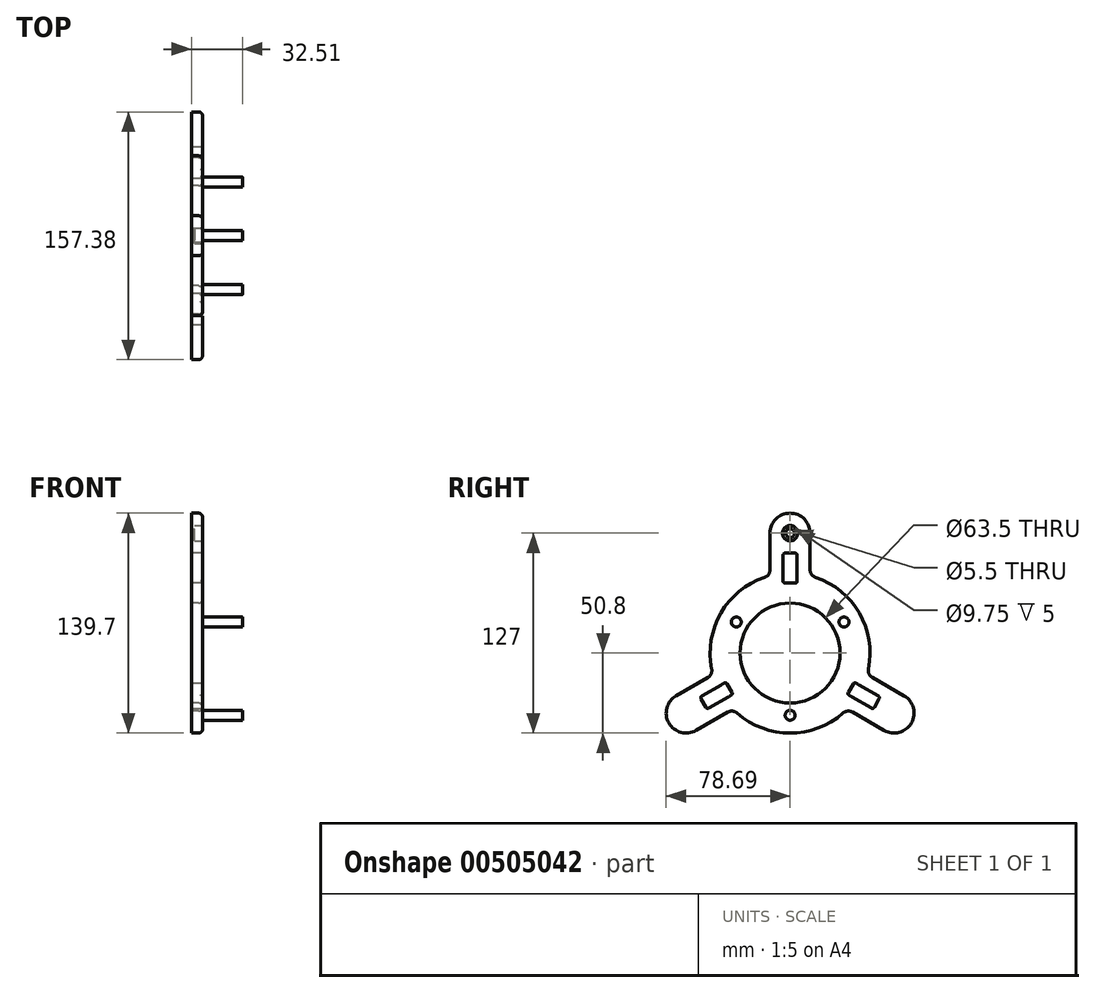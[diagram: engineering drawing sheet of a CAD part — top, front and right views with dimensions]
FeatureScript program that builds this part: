
annotation { "Feature Type Name" : "Feature", "Feature Type Description" : "" }
export const myFeature = defineFeature(function(context is Context, id is Id, definition is map)
    precondition{}
    {
        {
            var Q0;
            Q0=qCreatedBy(makeId("Right.planeOp"),FACE);
            var sketch = newSketch(context, id + "F0", { "sketchPlane" : qUnion([Q0])});
            skCircle(sketch, "E0", {"center": v(0, 0) * mm, "radius": 50.8 * mm});
            skCircle(sketch, "E1", {"center": v(0, 76.2) * mm, "radius": 12.7 * mm});
            skLineSegment(sketch, "E2", {"start": v(12.7, 76.2) * mm, "end": v(12.7, 49.19) * mm});
            skLineSegment(sketch, "E3", {"start": v(-12.7, 76.2) * mm, "end": v(-12.7, 49.19) * mm});
            skCircle(sketch, "E4", {"center": v(0, 0) * mm, "radius": 31.75 * mm});
            skLineSegment(sketch, "E5", {"start": v(0, 76.2) * mm, "end": v(0, 31.75) * mm});
            skLineSegment(sketch, "E6.bottom", {"start": v(4.45, 63.5) * mm, "end": v(-4.45, 63.5) * mm});
            skLineSegment(sketch, "E6.top", {"start": v(4.45, 44.45) * mm, "end": v(-4.45, 44.45) * mm});
            skLineSegment(sketch, "E6.left", {"start": v(4.45, 63.5) * mm, "end": v(4.45, 44.45) * mm});
            skLineSegment(sketch, "E6.right", {"start": v(-4.45, 63.5) * mm, "end": v(-4.45, 44.45) * mm});
            skPoint(sketch, "E6.middle", {"position": v(0, 53.98) * mm});
            skSolve(sketch);
        }
        {
            var Q0;
            {var subQ0=sQuery(id+"F0.wireOp",EDGE,"E0");var subQ1=makeQuery(id+"F0.imprint","INTERSECT",VERTEX,{"derivedFrom":[subQ0,sQuery(id+"F0.wireOp",EDGE,"E2")]});Q0=makeQuery(id+"F0.imprint","IMPRINT",FACE,{"disambiguationData":[TD([[makeQuery(id+"F0.imprint","IMPRINT",EDGE,{"disambiguationData":[TD([[subQ1,-1.0]])],"derivedFrom":subQ0}),1.0]])]});}
            var Q1;
            {var subQ0=sQuery(id+"F0.wireOp",EDGE,"E2");Q1=makeQuery(id+"F0.imprint","IMPRINT",FACE,{"disambiguationData":[TD([[makeQuery(id+"F0.imprint","IMPRINT",EDGE,{"derivedFrom":subQ0}),-1.0]])]});}
            var Q2;
            {var subQ0=sQuery(id+"F0.wireOp",EDGE,"E1");var subQ1=makeQuery(id+"F0.imprint","INTERSECT",VERTEX,{"derivedFrom":[subQ0,sQuery(id+"F0.wireOp",EDGE,"E2")]});Q2=makeQuery(id+"F0.imprint","IMPRINT",FACE,{"disambiguationData":[TD([[makeQuery(id+"F0.imprint","IMPRINT",EDGE,{"disambiguationData":[TD([[subQ1,-1.0]])],"derivedFrom":subQ0}),1.0]])]});}
            var Q3;
            {var subQ0=sQuery(id+"F0.wireOp",EDGE,"b7OHnpGz-8ywc-knMQ-bxzY-wuBPayrR5RMl");Q3=makeQuery(id+"F0.imprint","IMPRINT",FACE,{"disambiguationData":[TD([[makeQuery(id+"F0.imprint","IMPRINT",EDGE,{"derivedFrom":subQ0}),1.0]])]});}
            var Q4;
            {var subQ0=sQuery(id+"F0.wireOp",EDGE,"xrwcpAAF-OSON-ZUx1-X68L-PDSKPu6AwuQr");var subQ1=makeQuery(id+"F0.imprint","INTERSECT",VERTEX,{"derivedFrom":[subQ0,sQuery(id+"F0.wireOp",EDGE,"b7OHnpGz-8ywc-knMQ-bxzY-wuBPayrR5RMl")]});Q4=makeQuery(id+"F0.imprint","IMPRINT",FACE,{"disambiguationData":[TD([[makeQuery(id+"F0.imprint","IMPRINT",EDGE,{"disambiguationData":[TD([[subQ1,-1.0]])],"derivedFrom":subQ0}),1.0]])]});}
            var Q5;
            {var subQ0=sQuery(id+"F0.wireOp",EDGE,"RlsfpPi4-7fas-HaKM-YI3l-A7btP1uvOqbB");Q5=makeQuery(id+"F0.imprint","IMPRINT",FACE,{"disambiguationData":[TD([[makeQuery(id+"F0.imprint","IMPRINT",EDGE,{"derivedFrom":subQ0}),1.0]])]});}
            var Q6;
            {var subQ5=sQuery(id+"F0.wireOp",EDGE,"6OggtRER-jhK3-v4md-decp-ikiG6QNqgnZd");Q6=makeQuery(id+"F0.imprint","IMPRINT",FACE,{"disambiguationData":[TD([[makeQuery(id+"F0.imprint","IMPRINT",EDGE,{"derivedFrom":subQ5}),1.0]])]});}
            var Q7;
            {var subQ5=sQuery(id+"F0.wireOp",EDGE,"FEhqOE9T-DJEj-I29Y-v5rS-7Lfa6DwVfN2z.bottom");Q7=makeQuery(id+"F0.imprint","IMPRINT",FACE,{"disambiguationData":[TD([[makeQuery(id+"F0.imprint","IMPRINT",EDGE,{"derivedFrom":subQ5}),1.0]])]});}
            var Q8;
            {var subQ0=sQuery(id+"F0.wireOp",EDGE,"E3");Q8=makeQuery(id+"F0.imprint","IMPRINT",FACE,{"disambiguationData":[TD([[makeQuery(id+"F0.imprint","IMPRINT",EDGE,{"derivedFrom":subQ0}),1.0]])]});}
            extrude(context, id + "F1", {"entities" : qUnion([Q0, Q1, Q2, Q3, Q4, Q5, Q6, Q7, Q8]), "depth" : 7.11 * mm});
        }
        {
            var Q0;
            Q0=makeQuery(id+"F1.opExtrude","CAP_FACE",FACE,{"disambiguationData":[OSD([sQuery(id+"F0.wireOp",EDGE,"E0"),sQuery(id+"F0.wireOp",EDGE,"E1"),sQuery(id+"F0.wireOp",EDGE,"E2"),sQuery(id+"F0.wireOp",EDGE,"E3")])],"isStart":false});
            var sketch = newSketch(context, id + "F2", { "sketchPlane" : qUnion([Q0])});
            skPoint(sketch, "E7", {"position": v(0, 76.2) * mm});
            skSolve(sketch);
        }
        {
            var Q0;
            Q0=sQuery(id+"F2.wireOp",VERTEX,"E7");
            var Q1;
            Q1=makeQuery(id+"F1.opExtrude","SWEPT_BODY",BODY,{"disambiguationData":[OSD([sQuery(id+"F0.wireOp",EDGE,"E0"),sQuery(id+"F0.wireOp",EDGE,"E1"),sQuery(id+"F0.wireOp",EDGE,"E2"),sQuery(id+"F0.wireOp",EDGE,"E3")])]});
            hole(context, id + "F3", {"style" : HoleStyle.C_BORE, "endStyle" : HoleEndStyle.THROUGH, "standardTappedOrClearance" : lookupTablePath({ "standard" : "ISO", "fit" : "Normal", "size" : "M5", "type" : "Clearance" }), "standardBlindInLast" : lookupTablePath({ "fit" : "Standard", "standard" : "ISO", "size" : "M5", "type" : "Clearance" }), "holeDiameter" : 5.5 * mm, "cBoreDiameter" : 9.75 * mm, "cBoreDepth" : 5 * mm, "isTappedThrough" : true, "tappedDepth" : 12.7 * mm, "tapClearance" : 3, "locations" : qUnion([Q0]), "scope" : qUnion([Q1])});
        }
        {
            var Q0;
            Q0=makeQuery(id+"F1.opExtrude","SWEPT_EDGE",EDGE,{"disambiguationData":[OSD([sQuery(id+"F0.wireOp",EDGE,"E6.bottom"),sQuery(id+"F0.wireOp",EDGE,"E6.left")])]});
            var Q1;
            Q1=makeQuery(id+"F1.opExtrude","SWEPT_EDGE",EDGE,{"disambiguationData":[OSD([sQuery(id+"F0.wireOp",EDGE,"E6.bottom"),sQuery(id+"F0.wireOp",EDGE,"E6.right")])]});
            var Q2;
            Q2=makeQuery(id+"F1.opExtrude","SWEPT_EDGE",EDGE,{"disambiguationData":[OSD([sQuery(id+"F0.wireOp",EDGE,"E6.top"),sQuery(id+"F0.wireOp",EDGE,"E6.right")])]});
            var Q3;
            Q3=makeQuery(id+"F1.opExtrude","SWEPT_EDGE",EDGE,{"disambiguationData":[OSD([sQuery(id+"F0.wireOp",EDGE,"E6.top"),sQuery(id+"F0.wireOp",EDGE,"E6.left")])]});
            var Q4;
            Q4=makeQuery(id+"F1.opExtrude","CAP_EDGE",EDGE,{"disambiguationData":[OSD([sQuery(id+"F0.wireOp",EDGE,"E6.top")])],"isStart":false});
            var Q5;
            Q5=makeQuery(id+"F3.hole-0.boolean.opBoolean","COPY",EDGE,{"derivedFrom":makeQuery(id+"F3.hole-0.opRevolve","SWEPT_EDGE",EDGE,{"disambiguationData":[OSD([sQuery(id+"F3.hole-0.sketch.wireOp",EDGE,"cbore_start_line_2"),sQuery(id+"F3.hole-0.sketch.wireOp",EDGE,"cbore_start_line_3")])]})});
            fillet(context, id + "F4", {"entities" : qUnion([Q0, Q1, Q2, Q3, Q4, Q5]), "radius" : 1.27 * mm, "tangentPropagation" : true, "allowEdgeOverflow" : false});
        }
        {
            var Q0;
            Q0=makeQuery(id+"F1.opExtrude","SWEPT_EDGE",EDGE,{"disambiguationData":[OSD([sQuery(id+"F0.wireOp",EDGE,"E0"),sQuery(id+"F0.wireOp",EDGE,"E3")])]});
            var Q1;
            Q1=makeQuery(id+"F1.opExtrude","SWEPT_EDGE",EDGE,{"disambiguationData":[OSD([sQuery(id+"F0.wireOp",EDGE,"E0"),sQuery(id+"F0.wireOp",EDGE,"E2")])]});
            fillet(context, id + "F5", {"entities" : qUnion([Q0, Q1]), "radius" : 5.08 * mm, "tangentPropagation" : true, "allowEdgeOverflow" : false});
        }
        {
            var Q0;
            Q0=makeQuery(id+"F1.opExtrude","CAP_FACE",FACE,{"disambiguationData":[OSD([sQuery(id+"F0.wireOp",EDGE,"E0"),sQuery(id+"F0.wireOp",EDGE,"E1"),sQuery(id+"F0.wireOp",EDGE,"E2"),sQuery(id+"F0.wireOp",EDGE,"E3"),sQuery(id+"F0.wireOp",EDGE,"E4"),sQuery(id+"F0.wireOp",EDGE,"E6.bottom"),sQuery(id+"F0.wireOp",EDGE,"E6.top"),sQuery(id+"F0.wireOp",EDGE,"E6.left"),sQuery(id+"F0.wireOp",EDGE,"E6.right")])],"isStart":false});
            var sketch = newSketch(context, id + "F6", { "sketchPlane" : qUnion([Q0])});
            skCircle(sketch, "E8", {"center": v(0, -39.5) * mm, "radius": 3.17 * mm});
            skSolve(sketch);
        }
        {
            var Q0;
            Q0=makeQuery(id+"F6.imprint","IMPRINT",FACE,{"disambiguationData":[TD([[makeQuery(id+"F6.imprint","IMPRINT",EDGE,{"derivedFrom":sQuery(id+"F6.wireOp",EDGE,"E8")}),1.0]])]});
            extrude(context, id + "F7", {"entities" : qUnion([Q0]), "operationType" : NewBodyOperationType.ADD, "depth" : 25.4 * mm, "offsetDistance" : 25.4 * mm});
        }
        {
            var Q0;
            Q0=makeQuery(id+"F1.opExtrude","SWEPT_FACE",FACE,{"disambiguationData":[OSD([sQuery(id+"F0.wireOp",EDGE,"E2")])]});
            var Q1;
            Q1=makeQuery(id+"F1.opExtrude","SWEPT_FACE",FACE,{"disambiguationData":[OSD([sQuery(id+"F0.wireOp",EDGE,"E1")])]});
            var Q2;
            Q2=makeQuery(id+"F1.opExtrude","SWEPT_FACE",FACE,{"disambiguationData":[OSD([sQuery(id+"F0.wireOp",EDGE,"E3")])]});
            var Q3;
            Q3=makeQuery(id+"F3.hole-0.boolean.opBoolean","COPY",FACE,{"derivedFrom":makeQuery(id+"F3.hole-0.opRevolve","SWEPT_FACE",FACE,{"disambiguationData":[OSD([sQuery(id+"F3.hole-0.sketch.wireOp",EDGE,"cbore_start_line_1")])]})});
            var Q4;
            Q4=makeQuery(id+"F3.hole-0.boolean.opBoolean","COPY",FACE,{"derivedFrom":makeQuery(id+"F3.hole-0.opRevolve","SWEPT_FACE",FACE,{"disambiguationData":[OSD([sQuery(id+"F3.hole-0.sketch.wireOp",EDGE,"cbore_start_line_2")])]})});
            var Q5;
            Q5=makeQuery(id+"F3.hole-0.boolean.opBoolean","COPY",FACE,{"derivedFrom":makeQuery(id+"F3.hole-0.opRevolve","SWEPT_FACE",FACE,{"disambiguationData":[OSD([sQuery(id+"F3.hole-0.sketch.wireOp",EDGE,"core_line_2")])]})});
            var Q6;
            Q6=makeQuery(id+"F5.opFillet","BLEND_FACE",FACE,{"disambiguationData":[OSD([sQuery(id+"F0.wireOp",EDGE,"E0"),sQuery(id+"F0.wireOp",EDGE,"E2")])]});
            var Q7;
            Q7=makeQuery(id+"F5.opFillet","BLEND_FACE",FACE,{"disambiguationData":[OSD([sQuery(id+"F0.wireOp",EDGE,"E0"),sQuery(id+"F0.wireOp",EDGE,"E3")])]});
            var Q8;
            Q8=makeQuery(id+"F1.opExtrude","SWEPT_FACE",FACE,{"disambiguationData":[OSD([sQuery(id+"F0.wireOp",EDGE,"E6.right")])]});
            var Q9;
            Q9=makeQuery(id+"F4.opFillet","BLEND_FACE",FACE,{"disambiguationData":[OSD([sQuery(id+"F0.wireOp",EDGE,"E6.right")])]});
            var Q10;
            {var subQ0=sQuery(id+"F0.wireOp",EDGE,"E6.right");var subQ1=sQuery(id+"F0.wireOp",EDGE,"E6.bottom");Q10=makeQuery(id+"F4.opFillet","BLEND_FACE",FACE,{"disambiguationData":[OSD([subQ1,subQ0]),TDD([makeQuery(id+"F1.opExtrude","CAP_VERTEX",VERTEX,{"disambiguationData":[OSD([subQ1,subQ0])],"isStart":false})])]});}
            var Q11;
            {var subQ0=sQuery(id+"F0.wireOp",EDGE,"E6.right");var subQ1=sQuery(id+"F0.wireOp",EDGE,"E6.bottom");Q11=makeQuery(id+"F4.opFillet","BLEND_FACE",FACE,{"disambiguationData":[OSD([subQ1,subQ0]),TDD([makeQuery(id+"F1.opExtrude","SWEPT_EDGE",EDGE,{"disambiguationData":[OSD([subQ1,subQ0])]})])]});}
            var Q12;
            Q12=makeQuery(id+"F4.opFillet","BLEND_FACE",FACE,{"disambiguationData":[OSD([sQuery(id+"F0.wireOp",EDGE,"E6.bottom")])]});
            var Q13;
            Q13=makeQuery(id+"F1.opExtrude","SWEPT_FACE",FACE,{"disambiguationData":[OSD([sQuery(id+"F0.wireOp",EDGE,"E6.bottom")])]});
            var Q14;
            {var subQ0=sQuery(id+"F0.wireOp",EDGE,"E6.left");var subQ1=sQuery(id+"F0.wireOp",EDGE,"E6.bottom");Q14=makeQuery(id+"F4.opFillet","BLEND_FACE",FACE,{"disambiguationData":[OSD([subQ1,subQ0]),TDD([makeQuery(id+"F1.opExtrude","SWEPT_EDGE",EDGE,{"disambiguationData":[OSD([subQ1,subQ0])]})])]});}
            var Q15;
            {var subQ0=sQuery(id+"F0.wireOp",EDGE,"E6.left");var subQ1=sQuery(id+"F0.wireOp",EDGE,"E6.bottom");Q15=makeQuery(id+"F4.opFillet","BLEND_FACE",FACE,{"disambiguationData":[OSD([subQ1,subQ0]),TDD([makeQuery(id+"F1.opExtrude","CAP_VERTEX",VERTEX,{"disambiguationData":[OSD([subQ1,subQ0])],"isStart":false})])]});}
            var Q16;
            Q16=makeQuery(id+"F4.opFillet","BLEND_FACE",FACE,{"disambiguationData":[OSD([sQuery(id+"F0.wireOp",EDGE,"E6.left")])]});
            var Q17;
            Q17=makeQuery(id+"F1.opExtrude","SWEPT_FACE",FACE,{"disambiguationData":[OSD([sQuery(id+"F0.wireOp",EDGE,"E6.left")])]});
            var Q18;
            {var subQ0=sQuery(id+"F0.wireOp",EDGE,"E6.left");var subQ1=sQuery(id+"F0.wireOp",EDGE,"E6.top");Q18=makeQuery(id+"F4.opFillet","BLEND_FACE",FACE,{"disambiguationData":[OSD([subQ1,subQ0]),TDD([makeQuery(id+"F1.opExtrude","CAP_VERTEX",VERTEX,{"disambiguationData":[OSD([subQ1,subQ0])],"isStart":false})])]});}
            var Q19;
            {var subQ0=sQuery(id+"F0.wireOp",EDGE,"E6.left");var subQ1=sQuery(id+"F0.wireOp",EDGE,"E6.top");Q19=makeQuery(id+"F4.opFillet","BLEND_FACE",FACE,{"disambiguationData":[OSD([subQ1,subQ0]),TDD([makeQuery(id+"F1.opExtrude","SWEPT_EDGE",EDGE,{"disambiguationData":[OSD([subQ1,subQ0])]})])]});}
            var Q20;
            Q20=makeQuery(id+"F1.opExtrude","SWEPT_FACE",FACE,{"disambiguationData":[OSD([sQuery(id+"F0.wireOp",EDGE,"E6.top")])]});
            var Q21;
            Q21=makeQuery(id+"F4.opFillet","BLEND_FACE",FACE,{"disambiguationData":[OSD([sQuery(id+"F0.wireOp",EDGE,"E6.top")])]});
            var Q22;
            {var subQ0=sQuery(id+"F0.wireOp",EDGE,"E6.right");var subQ1=sQuery(id+"F0.wireOp",EDGE,"E6.top");Q22=makeQuery(id+"F4.opFillet","BLEND_FACE",FACE,{"disambiguationData":[OSD([subQ1,subQ0]),TDD([makeQuery(id+"F1.opExtrude","CAP_VERTEX",VERTEX,{"disambiguationData":[OSD([subQ1,subQ0])],"isStart":false})])]});}
            var Q23;
            {var subQ0=sQuery(id+"F0.wireOp",EDGE,"E6.right");var subQ1=sQuery(id+"F0.wireOp",EDGE,"E6.top");Q23=makeQuery(id+"F4.opFillet","BLEND_FACE",FACE,{"disambiguationData":[OSD([subQ1,subQ0]),TDD([makeQuery(id+"F1.opExtrude","SWEPT_EDGE",EDGE,{"disambiguationData":[OSD([subQ1,subQ0])]})])]});}
            var Q24;
            Q24=makeQuery(id+"F4.opFillet","BLEND_FACE",FACE,{"disambiguationData":[OSD([sQuery(id+"F3.hole-0.sketch.wireOp",EDGE,"cbore_start_line_2"),sQuery(id+"F3.hole-0.sketch.wireOp",EDGE,"cbore_start_line_3")])]});
            var Q25;
            Q25=makeQuery(id+"F7.opExtrude","SWEPT_FACE",FACE,{"disambiguationData":[OSD([sQuery(id+"F6.wireOp",EDGE,"E8")])]});
            var Q26;
            Q26=makeQuery(id+"F1.opExtrude","SWEPT_FACE",FACE,{"disambiguationData":[OSD([sQuery(id+"F0.wireOp",EDGE,"E0")])]});
            circularPattern(context, id + "F8", {"patternType" : PatternType.FACE, "faces" : qUnion([Q0, Q1, Q2, Q3, Q4, Q5, Q6, Q7, Q8, Q9, Q10, Q11, Q12, Q13, Q14, Q15, Q16, Q17, Q18, Q19, Q20, Q21, Q22, Q23, Q24, Q25]), "axis" : qUnion([Q26]), "angle" : 360 * degree, "instanceCount" : 3, "equalSpace" : true});
        }
        {
            var Q0;
            Q0=makeQuery(id+"F1.opExtrude","CAP_EDGE",EDGE,{"disambiguationData":[OSD([sQuery(id+"F0.wireOp",EDGE,"E3")])],"isStart":false});
            var Q1;
            Q1=makeQuery(id+"F1.opExtrude","CAP_EDGE",EDGE,{"disambiguationData":[OSD([sQuery(id+"F0.wireOp",EDGE,"E4")])],"isStart":false});
            fillet(context, id + "F9", {"entities" : qUnion([Q0, Q1]), "radius" : 2.54 * mm, "tangentPropagation" : true, "allowEdgeOverflow" : false});
        }
    });
